# Revit family: Domotics-DomesticRanges-GEWISS-SYSTEM_SIGNALLING-LAMP_DOUBLE_1M
name_source: partatom
category: Apparecchi elettrici
revit_build: Autodesk Revit 2016 (Build: 20161004_0715(x64)
units: mm (PartAtom-declared; Revit-internal decimal feet)

## family parameters
Condiviso = Sì
Host = Superficie
Mantenere orientamento annotazione = Sì
Punto di calcolo locali = Sì
Quota connettore circolare = Usa diametro
Taglio con vuoti quando caricato = Sì
Tipo di parte = Normale

## types (4) — shared parameters
Carico apparente = 0 VA
Catalogue = DOMOTICS
Catalogue Range = SYSTEM - DOMESTIC RANGE
Description. = Double flat indicator lamp
Diffuser colour = Red/green
Diffuser colour: = Red/green
Diffusor type = Flat
Electrocod = 0132
IDF = fa8715cc-8835-4c7b-a9ed-edc2e44da95e
IDT = 7aee3e4a-9bac-4835-8ee0-70a5faa2074a
Immagine tipo = GW21608.jpg
N. poli = 1
No. SYSTEM modules = 1
Produttore = GEWISS S.p.A.
Prospetto di default = 1219 mm
SEO = Indicator
TIPO_ = System Spie Doppie 1M_GENERICO : GW21608 Spia segnalazione doppia rosso/verde 12/24V nero
Technical sheet = https://www.gewiss.com
Type = Double
Type: = Double
URL = https://www.gewiss.com
Version file RFA = 19.4
Volt = 230 V

## per-type parameters (varying)
| type | Colour | Descrizione | EAN code | Lamp voltage | Modello |
| GW21608 - Double ind.light-red/green 12/24V black | Black | DOUBLE IND.LIGHT-RED/GREEN 12/24V SY/BK | 8011564129757 | 12-24V ac/dc | GW21608 |
| GW20608 - Double ind.light-red/green 12/24V white | White | DOUBLE IND.LIGHT-RED/GREEN 12/24V SY/WT | 8011564001015 | 12-24V ac/dc | GW20608 |
| GW20607 - Double ind.light-red/green 230V white | White | DOUBLE IND.LIGHT-RED/GREEN 230V SY/WT | 8011564001008 | 230V ac | GW20607 |
| GW21607 - Double ind.light-red/green 230V black | Black | DOUBLE IND.LIGHT-RED/GREEN 230V SY/BK | 8011564129740 | 230V ac | GW21607 |

## geometry (parser evidence)
native form markers: Sweep x2
no freeform markers — native parametric forms only
